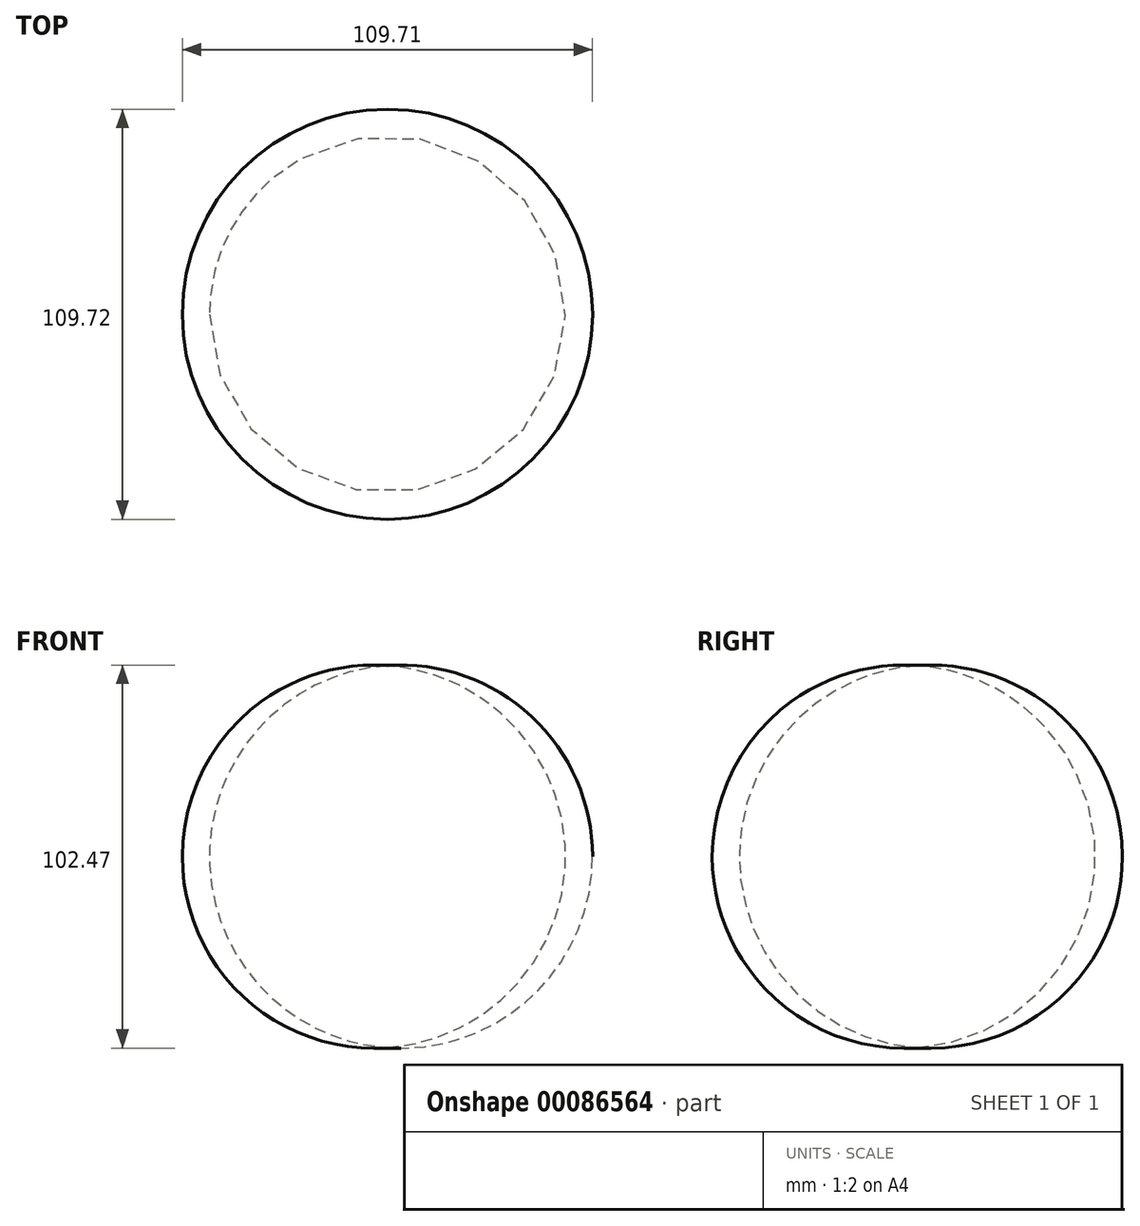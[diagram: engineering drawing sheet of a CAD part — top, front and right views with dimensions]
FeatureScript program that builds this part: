
annotation { "Feature Type Name" : "Feature", "Feature Type Description" : "" }
export const myFeature = defineFeature(function(context is Context, id is Id, definition is map)
    precondition{}
    {
        {
            var Q0;
            Q0=qCreatedBy(makeId("Front.planeOp"),FACE);
            var sketch = newSketch(context, id + "F0", { "sketchPlane" : qUnion([Q0])});
            skLineSegment(sketch, "E0", {"start": v(-57.51, 59.75) * mm, "end": v(-57.51, -42.46) * mm});
            skArc(sketch, "E1", {"start": v(-57.51, -42.46) * mm, "mid": v(-9.9, 8.64) * mm, "end": v(-57.51, 59.75) * mm});
            skSolve(sketch);
        }
        {
            var Q0;
            Q0 = qSketchRegion(id + "F0", true);
            var Q1;
            Q1=sQuery(id+"F0.wireOp",EDGE,"E0");
            revolve(context, id + "F1", {"entities" : qUnion([Q0]), "axis" : qUnion([Q1]), "revolveType" : RevolveType.FULL});
        }
    });
